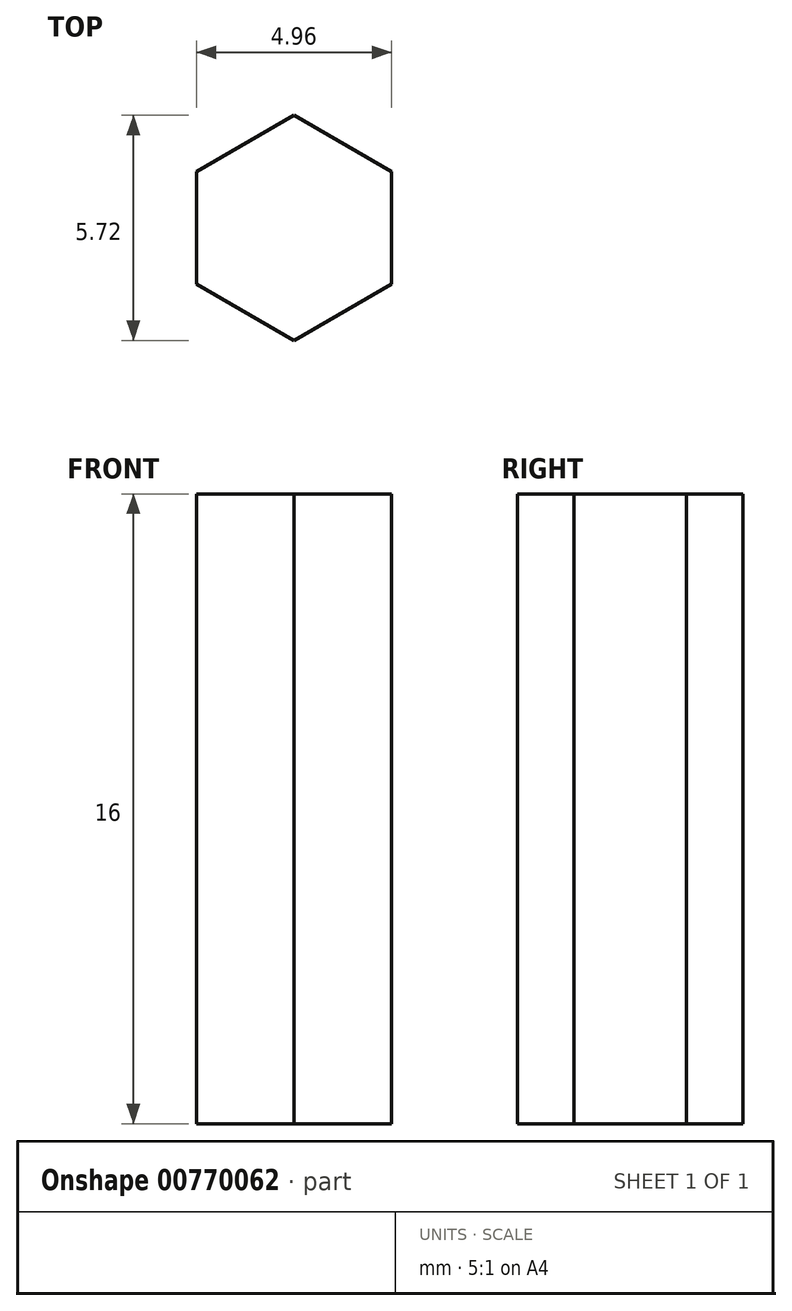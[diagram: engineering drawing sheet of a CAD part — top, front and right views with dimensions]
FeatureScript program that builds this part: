
annotation { "Feature Type Name" : "Feature", "Feature Type Description" : "" }
export const myFeature = defineFeature(function(context is Context, id is Id, definition is map)
    precondition{}
    {
        {
            var Q0;
            Q0=qCreatedBy(makeId("Top.planeOp"),FACE);
            var sketch = newSketch(context, id + "F0", { "sketchPlane" : qUnion([Q0])});
            skLineSegment(sketch, "E0", {"start": v(0, 0) * mm, "end": v(0, 4.01) * mm, "construction": true});
            skCircle(sketch, "E1.cCircle", {"center": v(0, 0) * mm, "radius": 2.48 * mm, "construction": true});
            skLineSegment(sketch, "E1.0", {"start": v(2.48, 1.43) * mm, "end": v(2.48, -1.43) * mm});
            skLineSegment(sketch, "E1.1", {"start": v(2.48, -1.43) * mm, "end": v(0, -2.86) * mm});
            skLineSegment(sketch, "E1.2", {"start": v(0, -2.86) * mm, "end": v(-2.48, -1.43) * mm});
            skLineSegment(sketch, "E1.3", {"start": v(-2.48, -1.43) * mm, "end": v(-2.48, 1.43) * mm});
            skLineSegment(sketch, "E1.4", {"start": v(-2.48, 1.43) * mm, "end": v(0, 2.86) * mm});
            skLineSegment(sketch, "E1.5", {"start": v(0, 2.86) * mm, "end": v(2.48, 1.43) * mm});
            skPoint(sketch, "E1.0.midPoint", {"position": v(2.48, 0) * mm});
            skSolve(sketch);
        }
        {
            var Q0;
            Q0=makeQuery(id+"F0.imprint","IMPRINT",FACE,{"disambiguationData":[TD([[makeQuery(id+"F0.imprint","IMPRINT",EDGE,{"derivedFrom":sQuery(id+"F0.wireOp",EDGE,"E1.0")}),-1.0]])]});
            extrude(context, id + "F1", {"entities" : qUnion([Q0]), "depth" : 16 * mm, "offsetDistance" : 25 * mm});
        }
    });
